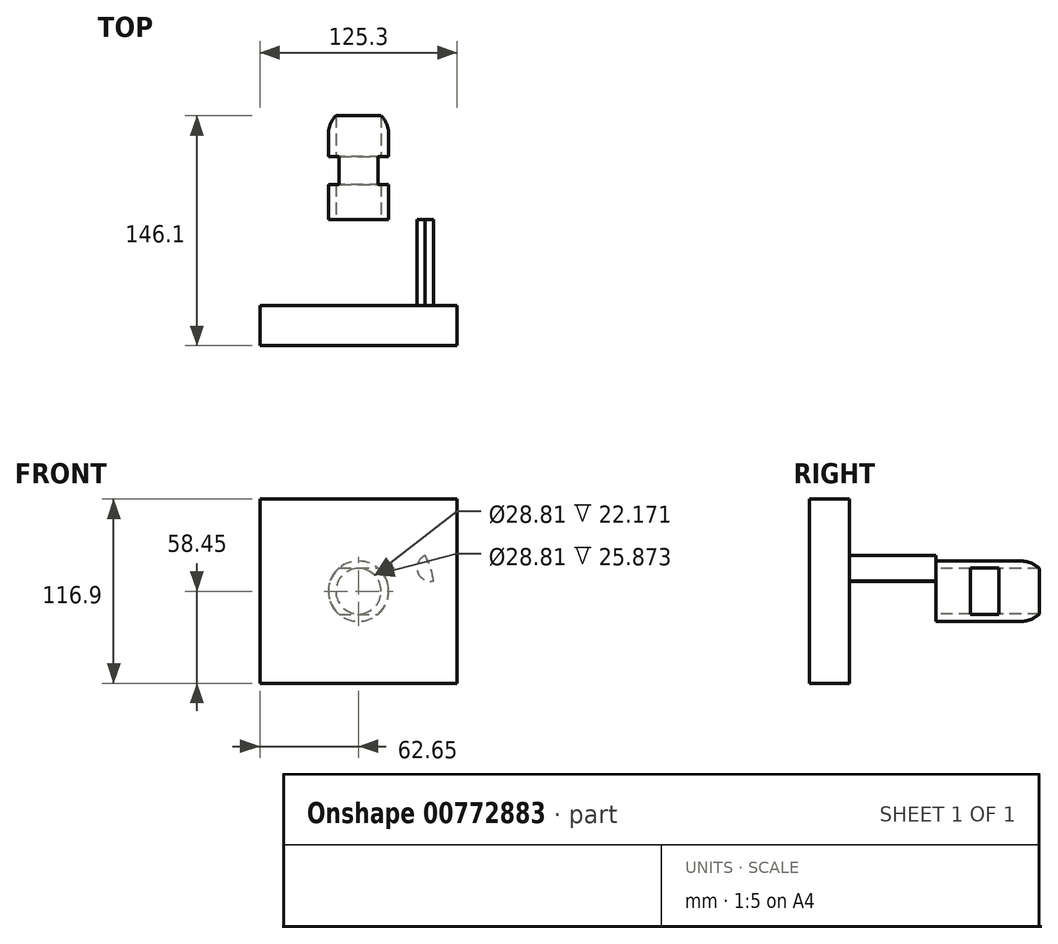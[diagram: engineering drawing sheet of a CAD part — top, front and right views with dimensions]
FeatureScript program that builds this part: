
annotation { "Feature Type Name" : "Feature", "Feature Type Description" : "" }
export const myFeature = defineFeature(function(context is Context, id is Id, definition is map)
    precondition{}
    {
        {
            var Q0;
            Q0=qCreatedBy(makeId("Front.planeOp"),FACE);
            var sketch = newSketch(context, id + "F0", { "sketchPlane" : qUnion([Q0])});
            skLineSegment(sketch, "E0.bottom", {"start": v(62.65, -58.45) * mm, "end": v(-62.65, -58.45) * mm});
            skLineSegment(sketch, "E0.top", {"start": v(62.65, 58.45) * mm, "end": v(-62.65, 58.45) * mm});
            skLineSegment(sketch, "E0.left", {"start": v(62.65, -58.45) * mm, "end": v(62.65, 58.45) * mm});
            skLineSegment(sketch, "E0.right", {"start": v(-62.65, -58.45) * mm, "end": v(-62.65, 58.45) * mm});
            skPoint(sketch, "E0.middle", {"position": v(0, 0) * mm});
            skSolve(sketch);
        }
        {
            var Q0;
            Q0 = qSketchRegion(id + "F0", true);
            var sketch = newSketch(context, id + "F1", { "sketchPlane" : qUnion([Q0])});
            skCircle(sketch, "E1", {"center": v(0, 0) * mm, "radius": 48.09 * mm});
            skCircle(sketch, "E2", {"center": v(0, 48.09) * mm, "radius": 8.57 * mm});
            skCircle(sketch, "E3.1.0", {"center": v(-45.73, 14.86) * mm, "radius": 8.57 * mm});
            skCircle(sketch, "E3.2.0", {"center": v(-28.27, -38.9) * mm, "radius": 8.57 * mm});
            skCircle(sketch, "E3.3.0", {"center": v(28.27, -38.9) * mm, "radius": 8.57 * mm});
            skCircle(sketch, "E3.4.0", {"center": v(45.73, 14.86) * mm, "radius": 8.57 * mm});
            skSolve(sketch);
        }
        {
            var Q0;
            Q0=makeQuery(id+"F0.imprint","IMPRINT",FACE,{"disambiguationData":[TD([[makeQuery(id+"F0.imprint","IMPRINT",EDGE,{"derivedFrom":sQuery(id+"F0.wireOp",EDGE,"E0.bottom")}),-1.0]])]});
            extrude(context, id + "F2", {"entities" : qUnion([Q0]), "depth" : 25.4 * mm, "offsetDistance" : 25.4 * mm});
        }
        {
            var Q0;
            {var subQ1=sQuery(id+"F1.wireOp",EDGE,"E1");var subQ5=sQuery(id+"F1.wireOp",EDGE,"E3.4.0");var subQ6=makeQuery(id+"F1.imprint","INTERSECT",VERTEX,{"disambiguationData":[OD(0.0)],"derivedFrom":[subQ1,subQ5]});Q0=makeQuery(id+"F1.imprint","IMPRINT",FACE,{"disambiguationData":[TD([[makeQuery(id+"F1.imprint","IMPRINT",EDGE,{"disambiguationData":[TD([[subQ6,-1.0]])],"derivedFrom":subQ1}),1.0]])]});}
            extrude(context, id + "F3", {"entities" : qUnion([Q0]), "operationType" : NewBodyOperationType.ADD, "oppositeDirection" : true, "depth" : 54.81 * mm, "offsetDistance" : 25.4 * mm});
        }
        {
            var Q0;
            Q0=makeQuery(id+"F3.opExtrude","CAP_FACE",FACE,{"disambiguationData":[OSD([sQuery(id+"F1.wireOp",EDGE,"E1"),sQuery(id+"F1.wireOp",EDGE,"E2"),sQuery(id+"F1.wireOp",EDGE,"E3.1.0"),sQuery(id+"F1.wireOp",EDGE,"E3.2.0"),sQuery(id+"F1.wireOp",EDGE,"E3.3.0"),sQuery(id+"F1.wireOp",EDGE,"E3.4.0")])],"isStart":false});
            var sketch = newSketch(context, id + "F4", { "sketchPlane" : qUnion([Q0])});
            skCircle(sketch, "E4", {"center": v(0, 0) * mm, "radius": 14.4 * mm});
            skCircle(sketch, "E5", {"center": v(0, 0) * mm, "radius": 19.14 * mm});
            skSolve(sketch);
        }
        {
            var Q0;
            Q0 = qSketchRegion(id + "F4", true);
            extrude(context, id + "F5", {"entities" : qUnion([Q0]), "operationType" : NewBodyOperationType.ADD, "depth" : 65.88 * mm, "offsetDistance" : 25.4 * mm});
        }
        {
            var Q0;
            Q0=makeQuery(id+"F5.opExtrude","CAP_EDGE",EDGE,{"disambiguationData":[OSD([sQuery(id+"F4.wireOp",EDGE,"E5")])],"isStart":false});
            fillet(context, id + "F6", {"entities" : qUnion([Q0]), "radius" : 16.82 * mm, "tangentPropagation" : true, "allowEdgeOverflow" : false});
        }
        {
            var Q0;
            Q0=qCreatedBy(makeId("Right.planeOp"),FACE);
            var sketch = newSketch(context, id + "F7", { "sketchPlane" : qUnion([Q0])});
            skLineSegment(sketch, "E6.bottom", {"start": v(94.82, -14.7) * mm, "end": v(76.98, -14.7) * mm});
            skLineSegment(sketch, "E6.top", {"start": v(94.82, 14.7) * mm, "end": v(76.98, 14.7) * mm});
            skLineSegment(sketch, "E6.left", {"start": v(94.82, -14.7) * mm, "end": v(94.82, 14.7) * mm});
            skLineSegment(sketch, "E6.right", {"start": v(76.98, -14.7) * mm, "end": v(76.98, 14.7) * mm});
            skPoint(sketch, "E6.middle", {"position": v(85.9, 0) * mm});
            skSolve(sketch);
        }
        {
            var Q0;
            Q0=makeQuery(id+"F7.imprint","IMPRINT",FACE,{"disambiguationData":[TD([[makeQuery(id+"F7.imprint","IMPRINT",EDGE,{"derivedFrom":sQuery(id+"F7.wireOp",EDGE,"E6.bottom")}),-1.0]])]});
            extrude(context, id + "F8", {"entities" : qUnion([Q0]), "operationType" : NewBodyOperationType.REMOVE, "oppositeDirection" : true, "depth" : 25.4 * mm, "offsetDistance" : 25.4 * mm, "hasSecondDirection" : true, "secondDirectionOppositeDirection" : false, "secondDirectionDepth" : 25.4 * mm});
        }
    });
